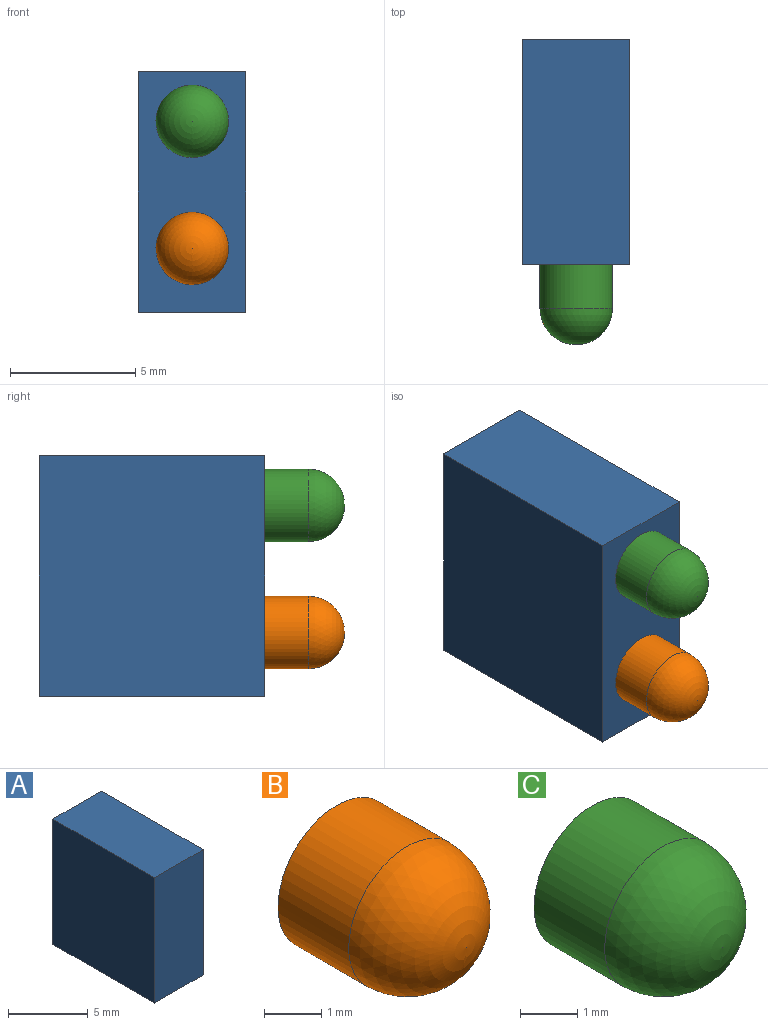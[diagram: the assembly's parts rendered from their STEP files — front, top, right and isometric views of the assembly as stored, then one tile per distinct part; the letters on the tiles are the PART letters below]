
ASSEMBLY  parts=3 mates=2
PART A: 6 faces, bbox 4.3x9x9.6 mm
  f0: plane 9x4.3mm, normal (0,0,1), area 38.7mm2, adj f1,f3,f4,f5
  f1: plane 9.6x9mm, normal (-1,0,0), area 86.4mm2, adj f0,f2,f4,f5
  f2: plane 9x4.3mm, normal (0,0,-1), area 38.7mm2, adj f1,f3,f4,f5
  f3: plane 9.6x9mm, normal (1,0,0), area 86.4mm2, adj f0,f2,f4,f5
  f4: plane 9.6x4.3mm, normal (0,1,0), area 41.3mm2, adj f0,f1,f2,f3
  f5: plane 9.6x4.3mm, normal (0,-1,0), area 41.3mm2, adj f0,f1,f2,f3
PART B: 3 faces, bbox 2.9x3.2x2.9 mm
  f0: sphere r=1.45mm, area 13.2mm2, adj f1
  f1: cylinder r=1.45mm len=2.9mm, axis (0,-1,0), area 15.9mm2, adj f0,f2
  f2: plane 2.9x2.9mm, normal (0,1,0), area 6.6mm2, adj f1
PART C: 3 faces, bbox 2.9x3.2x2.9 mm
  f0: sphere r=1.45mm, area 13.2mm2, adj f1
  f1: cylinder r=1.45mm len=2.9mm, axis (0,-1,0), area 15.9mm2, adj f0,f2
  f2: plane 2.9x2.9mm, normal (0,1,0), area 6.6mm2, adj f1
PLACE A t=(19.11,44.18,6.42)mm
PLACE B t=(19.13,44.18,6.66)mm
PLACE C t=(19.13,44.18,6.74)mm
MATE planar B.f1 <-> A.f5  axis (0,-1,0) through (19.11,35.18,4.14)mm
MATE planar C.f1 <-> A.f5  axis (0,1,0) through (19.11,35.18,9.22)mm
